# Revit family: CF-5_GENERADO
name_source: partatom
category: Equipos mecánicos
revit_build: Autodesk Revit 2014 (Build: 20130308_1515(x64)
units: mm (PartAtom-declared; Revit-internal decimal feet)

## types (3) — shared parameters
Comentarios de tipo = Ideal to make perfect french fries for restaurants and large kitchens.
Depth = 512 mm  [stored 1.67979 ft]
Fabricante = SAMMIC S.L.
Foodservice Equipment Identifier = Sí
Height = 735 mm  [stored 2.41142 ft]
Revision Code = 1
Specification by Manufacturer = Output: 100 - 150 Kg./h.
URL = https://www.sammic.com
URL Cutsheet = http://www.sammic.com
Weight in Pounds = 8.8
Width = 280 mm  [stored 0.918635 ft]

## per-type parameters (varying)
| type | Modelo |
| Hand chipping machine CF-5 · 8 x  8 mm (5/16" x 5/16") | 1020060 |
| Hand chipping machine CF-5 · 10 x 10 mm (⅜" x ⅜") | 1020061 |
| Hand chipping machine CF-5 · 12 x 12 mm  (½" x ½") | 1020062 |

note: column(s) folded — value = type name in every type: Descripción

note: [stored X ft] marks values corroborated as IEEE doubles in the binary element streams (Revit-internal decimal feet)
